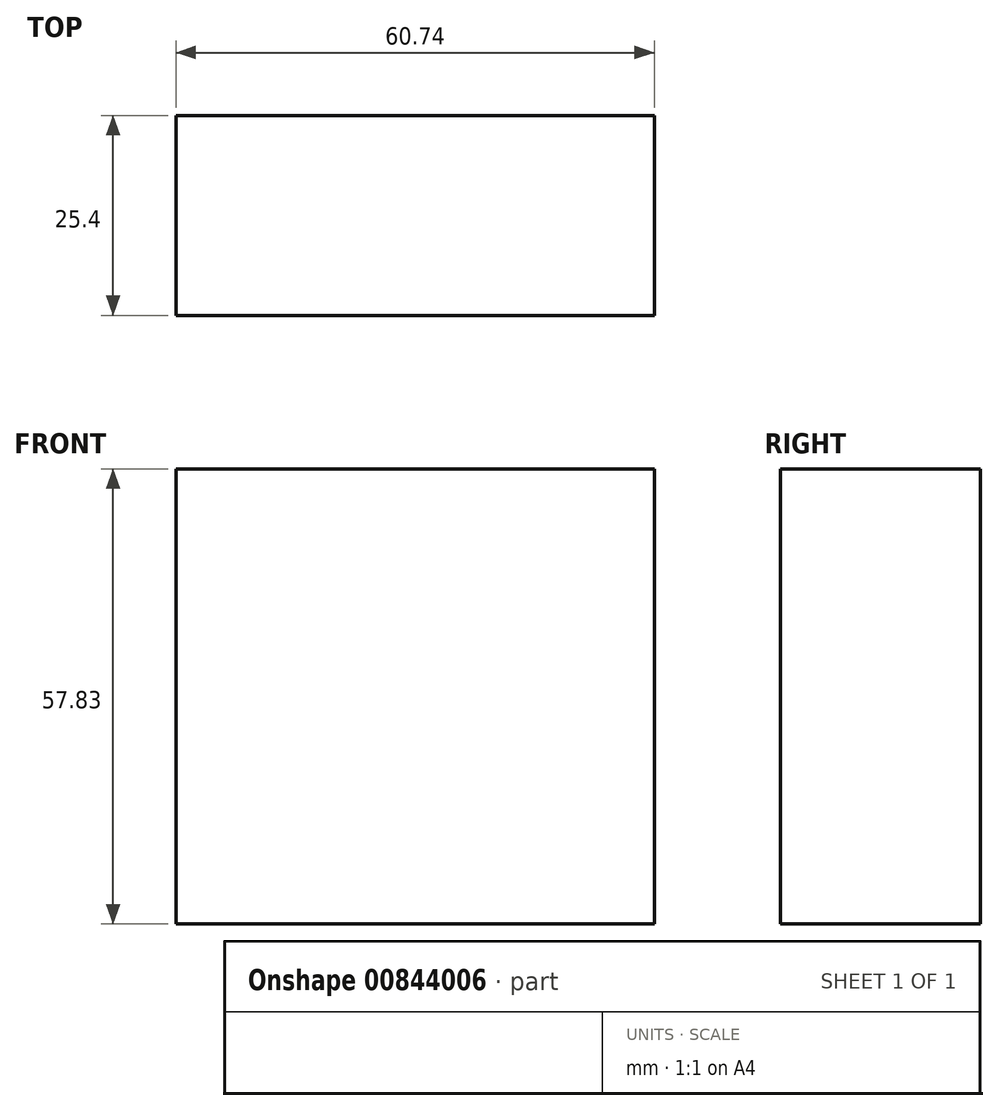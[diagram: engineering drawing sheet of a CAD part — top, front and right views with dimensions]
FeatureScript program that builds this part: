
annotation { "Feature Type Name" : "Feature", "Feature Type Description" : "" }
export const myFeature = defineFeature(function(context is Context, id is Id, definition is map)
    precondition{}
    {
        {
            var Q0;
            Q0=qCreatedBy(makeId("Front.planeOp"),FACE);
            var sketch = newSketch(context, id + "F0", { "sketchPlane" : qUnion([Q0])});
            skLineSegment(sketch, "E0.bottom", {"start": v(0, 0) * mm, "end": v(60.74, 0) * mm});
            skLineSegment(sketch, "E0.top", {"start": v(0, 57.83) * mm, "end": v(60.74, 57.83) * mm});
            skLineSegment(sketch, "E0.left", {"start": v(0, 0) * mm, "end": v(0, 57.83) * mm});
            skLineSegment(sketch, "E0.right", {"start": v(60.74, 0) * mm, "end": v(60.74, 57.83) * mm});
            skSolve(sketch);
        }
        {
            var Q0;
            Q0 = qSketchRegion(id + "F0", true);
            extrude(context, id + "F1", {"entities" : qUnion([Q0]), "depth" : 25.4 * mm, "offsetDistance" : 25.4 * mm});
        }
    });
